# Revit family: SD72W
name_source: partatom
category: Communication Devices
revit_build: Autodesk Revit 2014 (Build: 20140709_2115(x64)
units: mm (PartAtom-declared; Revit-internal decimal feet)

## types (1)
- In-Ceiling Loudspeaker
    25V Taps = .25, .5, 1, 2, & 5 Watts
    70V Taps = .25, .5, 1, 2, & 5 Watts
    Baffle Material = QF_Plastic - Black - Fine Textured
    Body Material = <By Category>
    Color = <By Category>
    Cost = 33.99 $
    Cost MSRP = 33.99 $
    Coverage = 105° (2kHz Octave Band, -6dB Points
    Coverage Horizontal = 110.00°
    Coverage Vertical = 110.00°
    Depth = 12 3/4"
    Description = 8" DUAL CONE IN-CEILING LOUDSPEAKER WITH 25V/70V 5-WATT TRANSFORMER AND 62-8 BAFFLE
    Dispersion Angle = 105.00°
    Enclosure Material = <By Category>
    Family Code (default) = LOUD SPEAKERS
    Frequency Response  = 55Hz - 19kHz (+/- 5dB)
    Grill Material = <By Category>
    Height = 2 7/8"
    IQ Category = SPEAKERS
    Impedance = 8
    Ingress Protection = IP-21
    Manufacturer = ATLAS SOUND
    Manufacturer URL = https://www.atlasied.com
    MasterFormat = 27 41 13
    MaterFormat Title = SPEAKERS
    Model = SD72W
    Mount Material = <By Category>
    OmniClass Number = 23-37 17 13 19
    OmniClass Title = SPEAKERS
    Power Rating (RMS) = 10 Watts
    Product Documentation Link = https://www.atlasied.com
    Product Page URL = https://www.atlasied.com
    SPL Max = 107
    ScheduleType |RF| = AtlasIED Master
    Sensitivity = 97
    Speaker Dispersion = 105.00°
    Speaker Type = S1
    Transformer Option = Yes
    URL = www.atlassound.com
    Vertical Symmetry = Yes
    Warranty = 5 Year
    Weight Product = 3.5
    Width = 12 3/4"

## geometry (parser evidence)
native form markers: Blend x10, Sweep x2
no freeform markers — native parametric forms only
